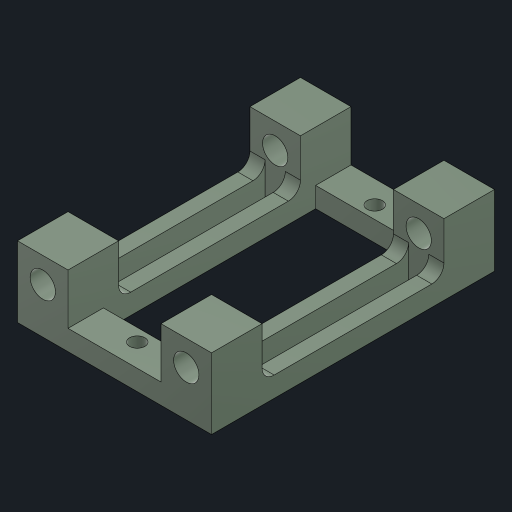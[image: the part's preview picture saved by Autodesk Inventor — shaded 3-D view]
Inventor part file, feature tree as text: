
AUTODESK INVENTOR PART (.ipt)
format: ipt  version: 2023 (Build 270158000, 158)  size: 233,984 bytes
history: native  units: in
note: dims shown in document units (in); Inventor stores cm internally (conversion verified against a paired STEP export)
features: sketch x4, extrude x4, other x3, mirror x2, hole x1, fillet x1, projected_geometry x1
ambient origin geometry x8: Origin, YZ Plane, XZ Plane, XY Plane, X Axis, Y Axis, Z Axis, Center Point
bodies: Body1 (feature_tree)
feature tree (16):
  other  "ソリッド1"
  sketch  "スケッチ1"
  extrude  "押し出し1"  Depth=0.8268in
  hole  "穴1"  [1 undecoded]
  extrude  "押し出し2"  Depth=0.1969in
  extrude  "押し出し5"  Depth=0.9252in
  mirror  "ミラー4"
  extrude  "押し出し6"  Depth=0.315in
  mirror  "ミラー5"
  fillet  "フィレット1"  Radius=0.0787in
  other  "作業平面1"
  other  "作業平面2"
  sketch  "スケッチ2"
  projected_geometry  "投影ループ1"
  sketch  "スケッチ6"
  sketch  "スケッチ7"
note: 1 required parameter value undecoded (feature->parameter linkage not recoverable at this tier; creation-order binding heuristic only, values carry confidence <= 0.55)
